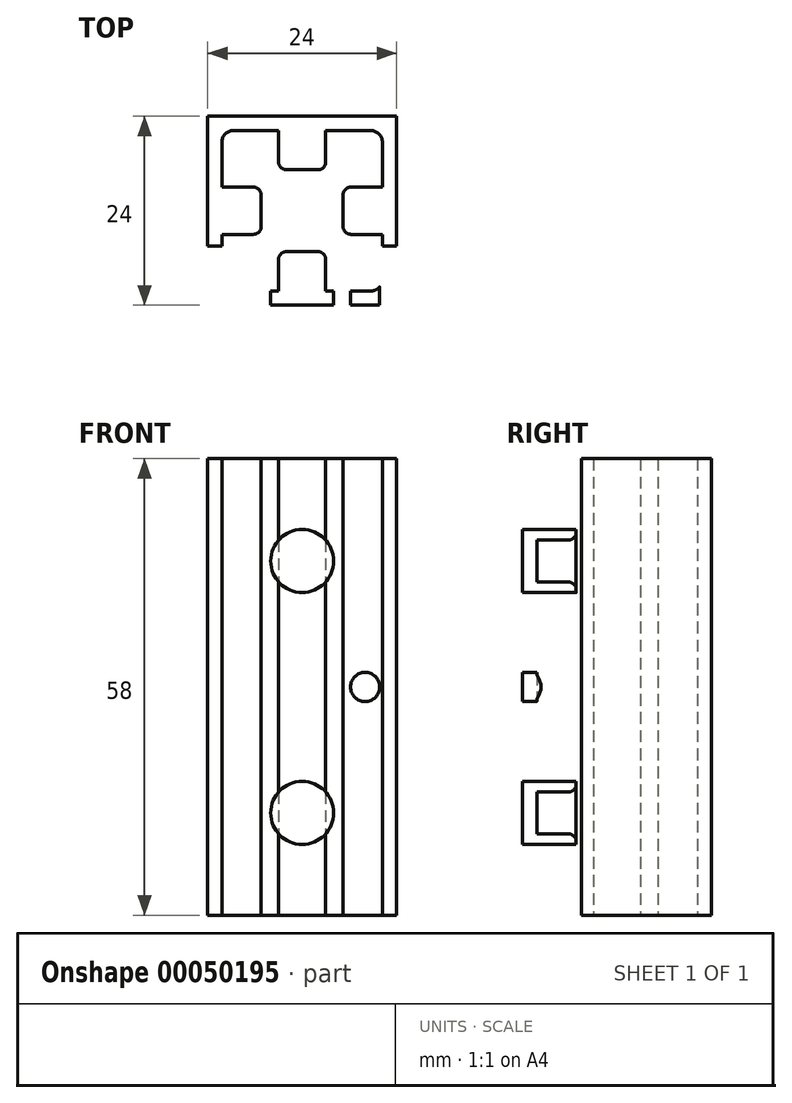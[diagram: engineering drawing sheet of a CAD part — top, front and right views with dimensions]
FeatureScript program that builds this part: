
annotation { "Feature Type Name" : "Feature", "Feature Type Description" : "" }
export const myFeature = defineFeature(function(context is Context, id is Id, definition is map)
    precondition{}
    {
        {
            var Q0;
            Q0=qCreatedBy(makeId("Top.planeOp"),FACE);
            var sketch = newSketch(context, id + "F0", { "sketchPlane" : qUnion([Q0])});
            skLineSegment(sketch, "E0.rect.bottom", {"start": v(-12, -12) * mm, "end": v(12, -12) * mm});
            skLineSegment(sketch, "E0.rect.top", {"start": v(-12, 12) * mm, "end": v(12, 12) * mm});
            skLineSegment(sketch, "E0.rect.left", {"start": v(-12, -12) * mm, "end": v(-12, 12) * mm});
            skLineSegment(sketch, "E0.rect.right", {"start": v(12, -12) * mm, "end": v(12, 12) * mm});
            skPoint(sketch, "E1.rect.middle", {"position": v(0, 0) * mm});
            skLineSegment(sketch, "E2", {"start": v(-10.2, -8.7) * mm, "end": v(-10.2, -3) * mm});
            skLineSegment(sketch, "E3.MirrorCS", {"start": v(-10.2, 8.7) * mm, "end": v(-10.2, 3) * mm});
            skLineSegment(sketch, "E4", {"start": v(-10.2, 3) * mm, "end": v(-6.2, 3) * mm});
            skLineSegment(sketch, "E5", {"start": v(-5.2, 2) * mm, "end": v(-5.2, -2) * mm});
            skLineSegment(sketch, "E6", {"start": v(-6.2, -3) * mm, "end": v(-10.2, -3) * mm});
            skPoint(sketch, "E7.visualSharp", {"position": v(-5.2, 3) * mm});
            skArc(sketch, "E7.filletArc", {"start": v(-5.2, 2) * mm, "mid": v(-5.5, 2.7) * mm, "end": v(-6.2, 3) * mm});
            skPoint(sketch, "E8.visualSharp", {"position": v(-5.2, -3) * mm});
            skArc(sketch, "E8.filletArc", {"start": v(-6.2, -3) * mm, "mid": v(-5.5, -2.7) * mm, "end": v(-5.2, -2) * mm});
            skPoint(sketch, "E9.visualSharp", {"position": v(-10.2, 10.2) * mm});
            skArc(sketch, "E9.filletArc", {"start": v(-8.7, 10.2) * mm, "mid": v(-9.76, 9.76) * mm, "end": v(-10.2, 8.7) * mm});
            skPoint(sketch, "E10.visualSharp", {"position": v(-10.2, -10.2) * mm});
            skArc(sketch, "E10.filletArc", {"start": v(-10.2, -8.7) * mm, "mid": v(-9.76, -9.76) * mm, "end": v(-8.7, -10.2) * mm});
            skPoint(sketch, "E11.1.1", {"position": v(3, -5.2) * mm});
            skLineSegment(sketch, "E11.1.2", {"start": v(-8.7, -10.2) * mm, "end": v(-3, -10.2) * mm});
            skLineSegment(sketch, "E11.1.3", {"start": v(8.7, -10.2) * mm, "end": v(3, -10.2) * mm});
            skPoint(sketch, "E11.1.4", {"position": v(10.2, -10.2) * mm});
            skLineSegment(sketch, "E11.1.5", {"start": v(3, -6.2) * mm, "end": v(3, -10.2) * mm});
            skArc(sketch, "E11.1.6", {"start": v(8.7, -10.2) * mm, "mid": v(9.76, -9.76) * mm, "end": v(10.2, -8.7) * mm});
            skLineSegment(sketch, "E11.1.7", {"start": v(-2, -5.2) * mm, "end": v(2, -5.2) * mm});
            skLineSegment(sketch, "E11.1.8", {"start": v(-3, -10.2) * mm, "end": v(-3, -6.2) * mm});
            skPoint(sketch, "E11.1.9", {"position": v(-3, -5.2) * mm});
            skArc(sketch, "E11.1.11", {"start": v(-2, -5.2) * mm, "mid": v(-2.7, -5.5) * mm, "end": v(-3, -6.2) * mm});
            skArc(sketch, "E11.1.12", {"start": v(3, -6.2) * mm, "mid": v(2.7, -5.5) * mm, "end": v(2, -5.2) * mm});
            skPoint(sketch, "E11.2.0", {"position": v(10.2, -10.2) * mm});
            skPoint(sketch, "E11.2.1", {"position": v(5.2, 3) * mm});
            skLineSegment(sketch, "E11.2.2", {"start": v(10.2, -8.7) * mm, "end": v(10.2, -3) * mm});
            skLineSegment(sketch, "E11.2.3", {"start": v(10.2, 8.7) * mm, "end": v(10.2, 3) * mm});
            skPoint(sketch, "E11.2.4", {"position": v(10.2, 10.2) * mm});
            skLineSegment(sketch, "E11.2.5", {"start": v(6.2, 3) * mm, "end": v(10.2, 3) * mm});
            skArc(sketch, "E11.2.6", {"start": v(10.2, 8.7) * mm, "mid": v(9.76, 9.76) * mm, "end": v(8.7, 10.2) * mm});
            skLineSegment(sketch, "E11.2.7", {"start": v(5.2, -2) * mm, "end": v(5.2, 2) * mm});
            skLineSegment(sketch, "E11.2.8", {"start": v(10.2, -3) * mm, "end": v(6.2, -3) * mm});
            skPoint(sketch, "E11.2.9", {"position": v(5.2, -3) * mm});
            skArc(sketch, "E11.2.10", {"start": v(8.7, -10.2) * mm, "mid": v(9.76, -9.76) * mm, "end": v(10.2, -8.7) * mm});
            skArc(sketch, "E11.2.11", {"start": v(5.2, -2) * mm, "mid": v(5.5, -2.7) * mm, "end": v(6.2, -3) * mm});
            skArc(sketch, "E11.2.12", {"start": v(6.2, 3) * mm, "mid": v(5.5, 2.7) * mm, "end": v(5.2, 2) * mm});
            skPoint(sketch, "E11.3.0", {"position": v(10.2, 10.2) * mm});
            skPoint(sketch, "E11.3.1", {"position": v(-3, 5.2) * mm});
            skLineSegment(sketch, "E11.3.2", {"start": v(8.7, 10.2) * mm, "end": v(3, 10.2) * mm});
            skLineSegment(sketch, "E11.3.3", {"start": v(-8.7, 10.2) * mm, "end": v(-3, 10.2) * mm});
            skLineSegment(sketch, "E11.3.5", {"start": v(-3, 6.2) * mm, "end": v(-3, 10.2) * mm});
            skLineSegment(sketch, "E11.3.7", {"start": v(2, 5.2) * mm, "end": v(-2, 5.2) * mm});
            skLineSegment(sketch, "E11.3.8", {"start": v(3, 10.2) * mm, "end": v(3, 6.2) * mm});
            skPoint(sketch, "E11.3.9", {"position": v(3, 5.2) * mm});
            skArc(sketch, "E11.3.10", {"start": v(10.2, 8.7) * mm, "mid": v(9.76, 9.76) * mm, "end": v(8.7, 10.2) * mm});
            skArc(sketch, "E11.3.11", {"start": v(2, 5.2) * mm, "mid": v(2.7, 5.5) * mm, "end": v(3, 6.2) * mm});
            skArc(sketch, "E11.3.12", {"start": v(-3, 6.2) * mm, "mid": v(-2.7, 5.5) * mm, "end": v(-2, 5.2) * mm});
            skSolve(sketch);
        }
        {
            var Q0;
            Q0=makeQuery(id+"F0.imprint","IMPRINT",FACE,{"disambiguationData":[TD([[makeQuery(id+"F0.imprint","IMPRINT",EDGE,{"derivedFrom":sQuery(id+"F0.wireOp",EDGE,"E0.rect.bottom")}),1.0]])]});
            extrude(context, id + "F1", {"entities" : qUnion([Q0]), "depth" : 58 * mm});
        }
        {
            var Q0;
            Q0=makeQuery(id+"F1.opExtrude","SWEPT_FACE",FACE,{"disambiguationData":[OSD([sQuery(id+"F0.wireOp",EDGE,"E0.rect.bottom")])]});
            var sketch = newSketch(context, id + "F2", { "sketchPlane" : qUnion([Q0])});
            skCircle(sketch, "E12", {"center": v(0, 5) * mm, "radius": 1.85 * mm});
            skCircle(sketch, "E13", {"center": v(0, 13) * mm, "radius": 4 * mm});
            skCircle(sketch, "E14.1.0", {"center": v(8, 13) * mm, "radius": 1.85 * mm});
            skCircle(sketch, "E14.2.0", {"center": v(0, 21) * mm, "radius": 1.85 * mm});
            skCircle(sketch, "E14.3.0", {"center": v(-8, 13) * mm, "radius": 1.85 * mm});
            skLineSegment(sketch, "E15", {"start": v(0, 13) * mm, "end": v(8, 13) * mm, "construction": true});
            skLineSegment(sketch, "E16", {"start": v(0, 13) * mm, "end": v(0, 5) * mm, "construction": true});
            skLineSegment(sketch, "E17", {"start": v(0, 5) * mm, "end": v(0, 0) * mm, "construction": true});
            skLineSegment(sketch, "E18.0.1.0", {"start": v(0, 45) * mm, "end": v(8, 45) * mm, "construction": true});
            skCircle(sketch, "E18.0.1.1", {"center": v(-8, 45) * mm, "radius": 1.85 * mm});
            skCircle(sketch, "E18.0.1.2", {"center": v(8, 45) * mm, "radius": 1.85 * mm});
            skCircle(sketch, "E18.0.1.3", {"center": v(0, 37) * mm, "radius": 1.85 * mm});
            skCircle(sketch, "E18.0.1.4", {"center": v(0, 45) * mm, "radius": 4 * mm});
            skPoint(sketch, "E18.0.1.5", {"position": v(0, 45) * mm});
            skLineSegment(sketch, "E18.0.1.6", {"start": v(0, 45) * mm, "end": v(0, 37) * mm, "construction": true});
            skCircle(sketch, "E18.0.1.7", {"center": v(0, 53) * mm, "radius": 1.85 * mm});
            skLineSegment(sketch, "E18.direction2", {"start": v(0, 13) * mm, "end": v(0, 45) * mm, "construction": true});
            skCircle(sketch, "E19", {"center": v(-8, 29) * mm, "radius": 1.85 * mm});
            skPoint(sketch, "E19.centerSnap0", {"position": v(0, 29) * mm});
            skCircle(sketch, "E20.MirrorC", {"center": v(8, 29) * mm, "radius": 1.85 * mm});
            skSolve(sketch);
        }
        {
            var Q0;
            Q0=makeQuery(id+"F2.imprint","IMPRINT",FACE,{"disambiguationData":[TD([[makeQuery(id+"F2.imprint","IMPRINT",EDGE,{"derivedFrom":sQuery(id+"F2.wireOp",EDGE,"E18.0.1.7")}),1.0]])]});
            var Q1;
            Q1=makeQuery(id+"F2.imprint","IMPRINT",FACE,{"disambiguationData":[TD([[makeQuery(id+"F2.imprint","IMPRINT",EDGE,{"derivedFrom":sQuery(id+"F2.wireOp",EDGE,"E18.0.1.2")}),1.0]])]});
            var Q2;
            Q2=makeQuery(id+"F2.imprint","IMPRINT",FACE,{"disambiguationData":[TD([[makeQuery(id+"F2.imprint","IMPRINT",EDGE,{"derivedFrom":sQuery(id+"F2.wireOp",EDGE,"E18.0.1.1")}),1.0]])]});
            var Q3;
            Q3=makeQuery(id+"F2.imprint","IMPRINT",FACE,{"disambiguationData":[TD([[makeQuery(id+"F2.imprint","IMPRINT",EDGE,{"derivedFrom":sQuery(id+"F2.wireOp",EDGE,"E18.0.1.3")}),1.0]])]});
            var Q4;
            Q4=makeQuery(id+"F2.imprint","IMPRINT",FACE,{"disambiguationData":[TD([[makeQuery(id+"F2.imprint","IMPRINT",EDGE,{"derivedFrom":sQuery(id+"F2.wireOp",EDGE,"E19")}),1.0]])]});
            var Q5;
            Q5=makeQuery(id+"F2.imprint","IMPRINT",FACE,{"disambiguationData":[TD([[makeQuery(id+"F2.imprint","IMPRINT",EDGE,{"derivedFrom":sQuery(id+"F2.wireOp",EDGE,"E14.2.0")}),1.0]])]});
            var Q6;
            Q6=makeQuery(id+"F2.imprint","IMPRINT",FACE,{"disambiguationData":[TD([[makeQuery(id+"F2.imprint","IMPRINT",EDGE,{"derivedFrom":sQuery(id+"F2.wireOp",EDGE,"E20.MirrorC")}),-1.0]])]});
            var Q7;
            Q7=makeQuery(id+"F2.imprint","IMPRINT",FACE,{"disambiguationData":[TD([[makeQuery(id+"F2.imprint","IMPRINT",EDGE,{"derivedFrom":sQuery(id+"F2.wireOp",EDGE,"E14.1.0")}),1.0]])]});
            var Q8;
            Q8=makeQuery(id+"F2.imprint","IMPRINT",FACE,{"disambiguationData":[TD([[makeQuery(id+"F2.imprint","IMPRINT",EDGE,{"derivedFrom":sQuery(id+"F2.wireOp",EDGE,"E14.3.0")}),1.0]])]});
            var Q9;
            Q9=makeQuery(id+"F2.imprint","IMPRINT",FACE,{"disambiguationData":[TD([[makeQuery(id+"F2.imprint","IMPRINT",EDGE,{"derivedFrom":sQuery(id+"F2.wireOp",EDGE,"E12")}),1.0]])]});
            extrude(context, id + "F3", {"entities" : qUnion([Q0, Q1, Q2, Q3, Q4, Q5, Q6, Q7, Q8, Q9]), "operationType" : NewBodyOperationType.REMOVE, "oppositeDirection" : true, "depth" : 7.5 * mm});
        }
    });
